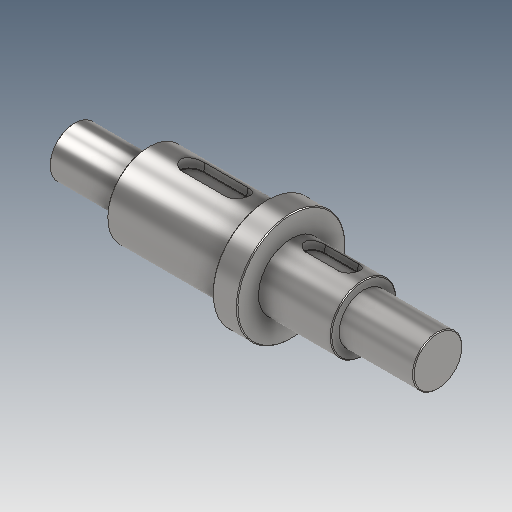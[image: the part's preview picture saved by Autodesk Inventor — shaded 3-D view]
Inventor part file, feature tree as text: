
AUTODESK INVENTOR PART (.ipt)
format: ipt  version: 2025 (Build 290162000, 162)  size: 276,992 bytes
history: native  units: mm
features: other x7, chamfer x6, revolve x1
ambient origin geometry x6: Origin, XZ Plane, XY Plane, X Axis, Y Axis, Z Axis
bodies: 实体1 (feature_tree)
feature tree (14):
  other  "{BB8FE430-83BF-418D-8DF9-9B323D3DB9B9}"
  revolve  "旋转1"  [1 undecoded]
  chamfer  "倒角6"  Distance=30.0mm
  chamfer  "倒角7"  Distance=50.0mm
  chamfer  "倒角1"  Distance=66.0mm
  chamfer  "倒角2"  Distance=40.0mm
  chamfer  "倒角3"  Distance=30.0mm
  chamfer  "倒角5"  [1 undecoded]
  other  "键槽3"
  other  "键槽4"
  other  "起始平面"
  other  "主草图"
  other  "轴键槽"
  other  "轴键槽2"
note: 2 required parameter values undecoded (feature->parameter linkage not recoverable at this tier; creation-order binding heuristic only, values carry confidence <= 0.55)